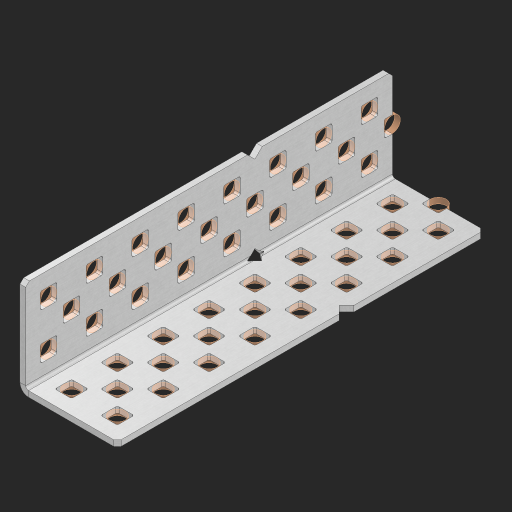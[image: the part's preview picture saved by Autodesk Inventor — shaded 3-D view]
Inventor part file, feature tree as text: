
AUTODESK INVENTOR PART (.ipt)
format: ipt  version: 2023 (Build 270158000, 158)  size: 901,120 bytes
history: native  units: in
note: dims shown in document units (in); Inventor stores cm internally (conversion verified against a paired STEP export)
features: other x54, extrude x46, sheet_metal_op x8, sketch x7, pattern_linear x2, mirror x1, chamfer x1
ambient origin geometry x8: Origin, YZ Plane, XZ Plane, XY Plane, X Axis, Y Axis, Z Axis, Center Point
bodies: Solid1 (feature_tree), Body (feature_tree)
feature tree (119):
  sheet_metal_op  "Flanges"
  sheet_metal_op  "Body Pattern"
  pattern_linear  "Center Pattern"  Spacing1=1.0in  [1 undecoded]
  other  "Arc Length"
  pattern_linear  "Notch Pattern"  Spacing1=0.25in  [1 undecoded]
  other  "Diagonal Plane"
  mirror  "Everything Mirrored"
  chamfer  "End Chamfer"
  sketch  "Sketch1"  dims[d0=1.0in]
  other  "Plate1"
  sketch  "Sketch2"  dims[d1=4.0in]
  other  "Plate2"
  sheet_metal_op  "Bend1"
  sheet_metal_op  "Corner1"
  sketch  "Sketch8"  dims[d2=0.0625in]
  sketch  "Sketch9"  dims[d3=0.0625in]
  other  "Srf91"
  sheet_metal_op  "Body Pattern Sketch"
  other  "Srf92"
  sketch  "Sketch13"  dims[d4=0.0312in]
  sketch  "Sketch15"  dims[d5=0.125in]
  sketch  "Sketch16"  dims[d6=0.0625in d7=1.0in d8=90.0deg d9=0.0312in d10=0.25in d11=0.0625in d12=0.0625in d49=0.182in d50=0.02in d52=0.25in d53=0.0625in d54=0.0in d55=0.172in d56=1.0in d57=0.0in d60=3.1496in d62=0.5in d63=0.7874in d65=0.5in d85=0.1473in d86=0.1782in d89=0.0625in d90=0.0in d91=0.04in d92=0.0491in d95=2.5in d96=0.04in d97=0.25in d98=45.0deg d99=0.25in d106=0.182in d107=0.02in d108=0.5in d110=0.0625in d111=0.0in d112=0.172in d113=0.5in d114=0.0in d117=0.5in d123=0.25in d125=0.25in d126=0.0491in d127=0.1473in d128=0.08in d129=0.04in d130=2.5in]
  other  "Srf786"
  other  "Srf856"
  other  "Srf857"
  other  "Srf858"
  other  "Srf859"
  other  "Srf860"
  other  "Srf861"
  other  "Srf889"
  other  "Srf890"
  other  "Srf891"
  other  "Srf1275"
  other  "Srf1276"
  other  "Srf1278"
  other  "Srf1279"
  other  "Srf1280"
  other  "Srf1281"
  other  "Srf1282"
  other  "Srf1283"
  other  "Srf1277"
  other  "Srf1285"
  other  "Srf1286"
  other  "Srf1287"
  other  "Srf1383"
  other  "Srf1384"
  other  "Srf1385"
  other  "Srf1386"
  other  "Srf1387"
  other  "Srf1388"
  other  "Srf1389"
  other  "Srf1390"
  other  "Srf1445"
  other  "Srf1446"
  other  "Srf1447"
  other  "Srf1448"
  other  "Srf1475"
  other  "Srf1476"
  other  "Srf1477"
  other  "Srf1478"
  other  "Srf1479"
  other  "Srf1480"
  other  "Srf1481"
  other  "Srf1482"
  other  "Srf1537"
  other  "Srf1538"
  other  "Srf1539"
  other  "Srf1540"
  sheet_metal_op  "Body Stamp"
  sheet_metal_op  "Body Circle"
  other  "Center Stamp"
  other  "Center Circle"
  sheet_metal_op  "Notch"
  extrude  "ExtrusionSrf92"  Depth=0.0625in
  extrude  "ExtrusionSrf856"  Depth=0.0625in
  extrude  "ExtrusionSrf857"  Depth=0.182in
  extrude  "ExtrusionSrf858"  Depth=0.02in
  extrude  "ExtrusionSrf859"  Depth=0.25in
  extrude  "ExtrusionSrf860"  Depth=0.0625in
  extrude  "ExtrusionSrf861"  TaperAngle=0.0deg  [1 undecoded]
  extrude  "ExtrusionSrf889"  Depth=2.5in
  extrude  "ExtrusionSrf890"  Depth=1.0in TaperAngle=0.0deg
  extrude  "ExtrusionSrf891"  Depth=2.5in
  extrude  "ExtrusionSrf1275"  Depth=0.5in
  extrude  "ExtrusionSrf1276"  Depth=2.5in
  extrude  "ExtrusionSrf1277"  Depth=2.5in
  extrude  "ExtrusionSrf1278"  Depth=0.0625in
  extrude  "ExtrusionSrf1279"  Depth=2.5in TaperAngle=0.0deg
  extrude  "ExtrusionSrf1280"  Depth=2.5in
  extrude  "ExtrusionSrf1281"  Depth=0.25in TaperAngle=45.0deg
  extrude  "ExtrusionSrf1282"  Depth=0.25in
  extrude  "ExtrusionSrf1345"  Depth=0.182in
  extrude  "ExtrusionSrf1346"  Depth=0.02in
  extrude  "ExtrusionSrf1347"  Depth=0.5in
  extrude  "ExtrusionSrf1348"  Depth=0.0625in
  extrude  "ExtrusionSrf1383"  TaperAngle=0.0deg  [1 undecoded]
  extrude  "ExtrusionSrf1384"  Depth=2.5in
  extrude  "ExtrusionSrf1385"  Depth=0.5in TaperAngle=0.0deg
  extrude  "ExtrusionSrf1386"  Depth=0.5in
  extrude  "ExtrusionSrf1387"  Depth=0.25in
  extrude  "ExtrusionSrf1388"  Depth=0.25in
  extrude  "ExtrusionSrf1389"  Depth=2.5in
  extrude  "ExtrusionSrf1390"  Depth=2.5in
  extrude  "ExtrusionSrf1445"  Depth=2.5in
  extrude  "ExtrusionSrf1446"  Depth=2.5in
  extrude  "ExtrusionSrf1447"  Depth=2.5in
  extrude  "ExtrusionSrf1448"  [1 undecoded]
  extrude  "ExtrusionSrf1475"  [1 undecoded]
  extrude  "ExtrusionSrf1476"  [1 undecoded]
  extrude  "ExtrusionSrf1477"  [1 undecoded]
  extrude  "ExtrusionSrf1478"  [1 undecoded]
  extrude  "ExtrusionSrf1479"  [1 undecoded]
  extrude  "ExtrusionSrf1480"  [1 undecoded]
  extrude  "ExtrusionSrf1481"  [1 undecoded]
  extrude  "ExtrusionSrf1482"  [1 undecoded]
  extrude  "ExtrusionSrf1537"  [1 undecoded]
  extrude  "ExtrusionSrf1538"  [1 undecoded]
  extrude  "ExtrusionSrf1539"  [1 undecoded]
  extrude  "ExtrusionSrf1540"  [1 undecoded]
note: 17 required parameter values undecoded (feature->parameter linkage not recoverable at this tier; creation-order binding heuristic only, values carry confidence <= 0.55)
